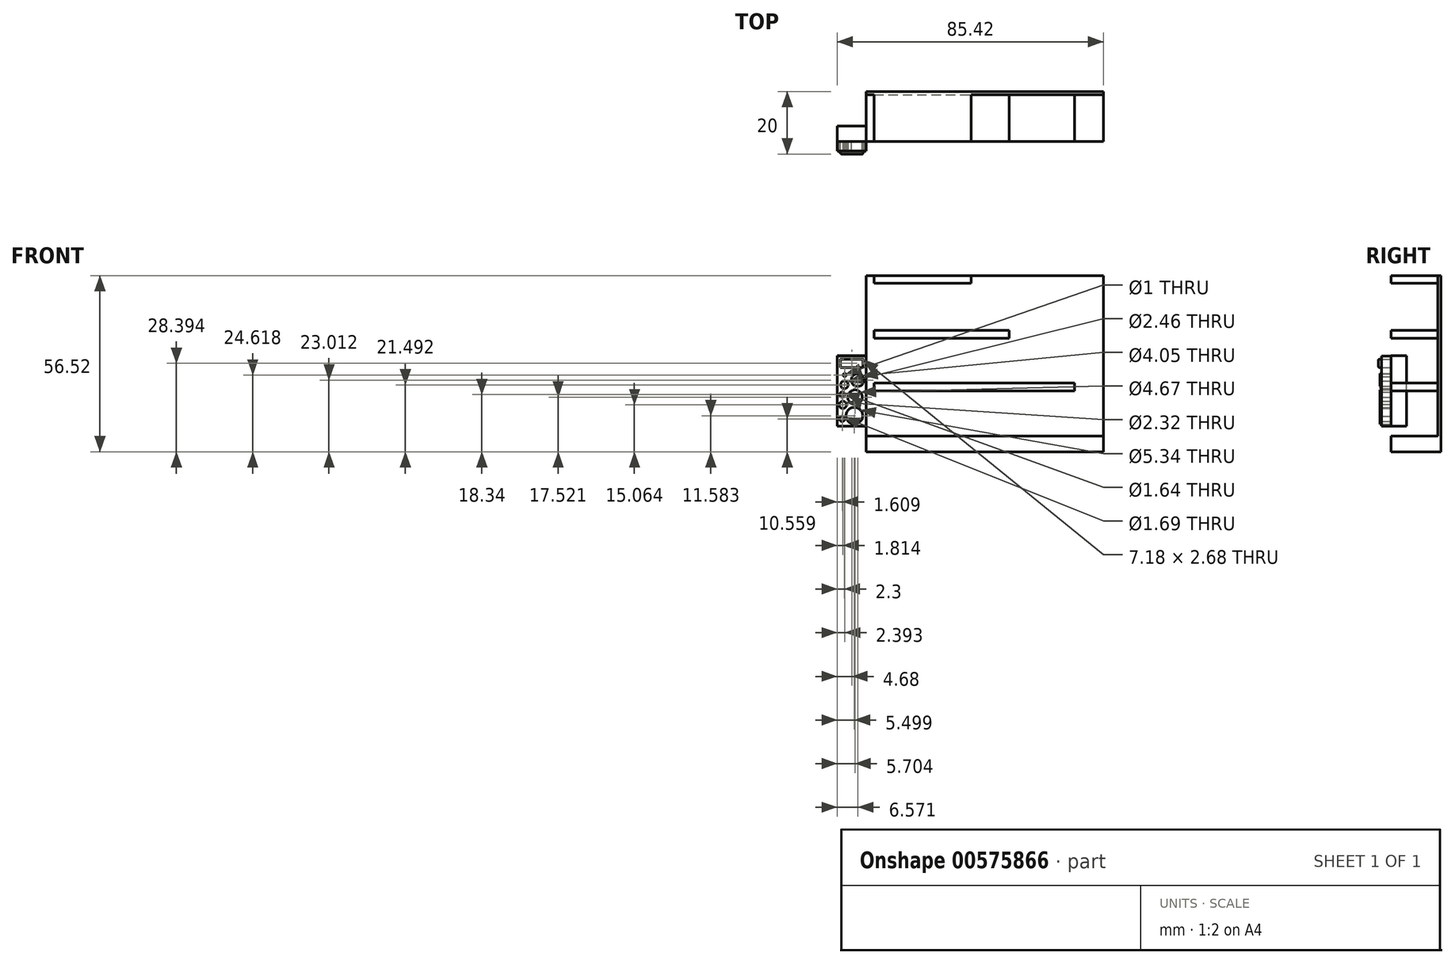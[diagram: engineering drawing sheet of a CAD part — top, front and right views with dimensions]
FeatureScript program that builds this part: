
annotation { "Feature Type Name" : "Feature", "Feature Type Description" : "" }
export const myFeature = defineFeature(function(context is Context, id is Id, definition is map)
    precondition{}
    {
        {
            var Q0;
            Q0=qCreatedBy(makeId("Front.planeOp"),FACE);
            var sketch = newSketch(context, id + "F0", { "sketchPlane" : qUnion([Q0])});
            skLineSegment(sketch, "E0.bottom", {"start": v(-35.88, 0.48) * mm, "end": v(40.2, 0.48) * mm});
            skLineSegment(sketch, "E0.top", {"start": v(-35.88, -4.52) * mm, "end": v(40.2, -4.52) * mm});
            skLineSegment(sketch, "E0.left", {"start": v(-35.88, 0.48) * mm, "end": v(-35.88, -4.52) * mm});
            skLineSegment(sketch, "E0.right", {"start": v(40.2, 0.48) * mm, "end": v(40.2, -4.52) * mm});
            skLineSegment(sketch, "E1.bottom", {"start": v(-35.88, 0.48) * mm, "end": v(-33.38, 0.48) * mm});
            skLineSegment(sketch, "E1.top", {"start": v(-35.88, 52) * mm, "end": v(-33.38, 52) * mm});
            skLineSegment(sketch, "E1.left", {"start": v(-35.88, 0.48) * mm, "end": v(-35.88, 52) * mm});
            skLineSegment(sketch, "E1.right", {"start": v(-33.38, 0.48) * mm, "end": v(-33.38, 52) * mm});
            skLineSegment(sketch, "E2.bottom", {"start": v(-33.38, 52) * mm, "end": v(-2.33, 52) * mm});
            skLineSegment(sketch, "E2.top", {"start": v(-33.38, 49.5) * mm, "end": v(-2.33, 49.5) * mm});
            skLineSegment(sketch, "E2.left", {"start": v(-33.38, 52) * mm, "end": v(-33.38, 49.5) * mm});
            skLineSegment(sketch, "E2.right", {"start": v(-2.33, 52) * mm, "end": v(-2.33, 49.5) * mm});
            skLineSegment(sketch, "E3.bottom", {"start": v(-33.38, 34.4) * mm, "end": v(9.95, 34.4) * mm});
            skLineSegment(sketch, "E3.top", {"start": v(-33.38, 31.9) * mm, "end": v(9.95, 31.9) * mm});
            skLineSegment(sketch, "E3.left", {"start": v(-33.38, 34.4) * mm, "end": v(-33.38, 31.9) * mm});
            skLineSegment(sketch, "E3.right", {"start": v(9.95, 34.4) * mm, "end": v(9.95, 31.9) * mm});
            skLineSegment(sketch, "E4.bottom", {"start": v(-33.38, 17.54) * mm, "end": v(30.82, 17.54) * mm});
            skLineSegment(sketch, "E4.top", {"start": v(-33.38, 15.04) * mm, "end": v(30.82, 15.04) * mm});
            skLineSegment(sketch, "E4.left", {"start": v(-33.38, 17.54) * mm, "end": v(-33.38, 15.04) * mm});
            skLineSegment(sketch, "E4.right", {"start": v(30.82, 17.54) * mm, "end": v(30.82, 15.04) * mm});
            skLineSegment(sketch, "E5.bottom", {"start": v(-35.88, 26.24) * mm, "end": v(-45.17, 26.24) * mm});
            skLineSegment(sketch, "E5.top", {"start": v(-35.88, 3.75) * mm, "end": v(-45.17, 3.75) * mm});
            skLineSegment(sketch, "E5.left", {"start": v(-35.88, 26.24) * mm, "end": v(-35.88, 3.75) * mm});
            skLineSegment(sketch, "E5.right", {"start": v(-45.17, 26.24) * mm, "end": v(-45.17, 3.75) * mm});
            skLineSegment(sketch, "E6.bottom", {"start": v(-44.12, 25.21) * mm, "end": v(-36.94, 25.21) * mm});
            skLineSegment(sketch, "E6.top", {"start": v(-44.12, 22.53) * mm, "end": v(-36.94, 22.53) * mm});
            skLineSegment(sketch, "E6.left", {"start": v(-44.12, 25.21) * mm, "end": v(-44.12, 22.53) * mm});
            skLineSegment(sketch, "E6.right", {"start": v(-36.94, 25.21) * mm, "end": v(-36.94, 22.53) * mm});
            skCircle(sketch, "E7", {"center": v(-42.82, 20.1) * mm, "radius": 0.5 * mm});
            skCircle(sketch, "E8", {"center": v(-42.9, 16.97) * mm, "radius": 1.23 * mm});
            skCircle(sketch, "E9", {"center": v(-38.64, 18.5) * mm, "radius": 2.03 * mm});
            skCircle(sketch, "E10", {"center": v(-39.5, 13) * mm, "radius": 2.33 * mm});
            skCircle(sketch, "E11", {"center": v(-43.4, 10.54) * mm, "radius": 1.16 * mm});
            skCircle(sketch, "E12", {"center": v(-39.71, 7.06) * mm, "radius": 2.67 * mm});
            skCircle(sketch, "E13", {"center": v(-43.6, 13.82) * mm, "radius": 0.82 * mm});
            skCircle(sketch, "E14", {"center": v(-43.6, 6.04) * mm, "radius": 0.84 * mm});
            skSolve(sketch);
        }
        {
            var Q0;
            Q0=makeQuery(id+"F0.imprint","IMPRINT",FACE,{"disambiguationData":[TD([[makeQuery(id+"F0.imprint","IMPRINT",EDGE,{"derivedFrom":sQuery(id+"F0.wireOp",EDGE,"E9")}),1.0]])]});
            var Q1;
            Q1=makeQuery(id+"F0.imprint","IMPRINT",FACE,{"disambiguationData":[TD([[makeQuery(id+"F0.imprint","IMPRINT",EDGE,{"derivedFrom":sQuery(id+"F0.wireOp",EDGE,"E7")}),1.0]])]});
            var Q2;
            Q2=makeQuery(id+"F0.imprint","IMPRINT",FACE,{"disambiguationData":[TD([[makeQuery(id+"F0.imprint","IMPRINT",EDGE,{"derivedFrom":sQuery(id+"F0.wireOp",EDGE,"E8")}),1.0]])]});
            var Q3;
            Q3=makeQuery(id+"F0.imprint","IMPRINT",FACE,{"disambiguationData":[TD([[makeQuery(id+"F0.imprint","IMPRINT",EDGE,{"derivedFrom":sQuery(id+"F0.wireOp",EDGE,"E10")}),1.0]])]});
            var Q4;
            Q4=makeQuery(id+"F0.imprint","IMPRINT",FACE,{"disambiguationData":[TD([[makeQuery(id+"F0.imprint","IMPRINT",EDGE,{"derivedFrom":sQuery(id+"F0.wireOp",EDGE,"E13")}),1.0]])]});
            var Q5;
            Q5=makeQuery(id+"F0.imprint","IMPRINT",FACE,{"disambiguationData":[TD([[makeQuery(id+"F0.imprint","IMPRINT",EDGE,{"derivedFrom":sQuery(id+"F0.wireOp",EDGE,"E11")}),1.0]])]});
            var Q6;
            Q6=makeQuery(id+"F0.imprint","IMPRINT",FACE,{"disambiguationData":[TD([[makeQuery(id+"F0.imprint","IMPRINT",EDGE,{"derivedFrom":sQuery(id+"F0.wireOp",EDGE,"E12")}),1.0]])]});
            var Q7;
            Q7=makeQuery(id+"F0.imprint","IMPRINT",FACE,{"disambiguationData":[TD([[makeQuery(id+"F0.imprint","IMPRINT",EDGE,{"derivedFrom":sQuery(id+"F0.wireOp",EDGE,"E14")}),1.0]])]});
            extrude(context, id + "F1", {"entities" : qUnion([Q0, Q1, Q2, Q3, Q4, Q5, Q6, Q7]), "depth" : 3.5 * mm, "offsetDistance" : 25.4 * mm});
        }
        {
            var Q0;
            Q0=makeQuery(id+"F0.imprint","IMPRINT",FACE,{"disambiguationData":[TD([[makeQuery(id+"F0.imprint","IMPRINT",EDGE,{"derivedFrom":sQuery(id+"F0.wireOp",EDGE,"E6.bottom")}),-1.0]])]});
            extrude(context, id + "F2", {"entities" : qUnion([Q0]), "depth" : 4 * mm, "offsetDistance" : 25.4 * mm});
        }
        {
            var Q0;
            Q0=makeQuery(id+"F0.imprint","IMPRINT",FACE,{"disambiguationData":[TD([[makeQuery(id+"F0.imprint","IMPRINT",EDGE,{"derivedFrom":sQuery(id+"F0.wireOp",EDGE,"E5.bottom")}),1.0]])]});
            extrude(context, id + "F3", {"entities" : qUnion([Q0]), "depth" : 3 * mm, "offsetDistance" : 25.4 * mm});
        }
        {
            var Q0;
            Q0=makeQuery(id+"F0.imprint","IMPRINT",FACE,{"disambiguationData":[TD([[makeQuery(id+"F0.imprint","IMPRINT",EDGE,{"derivedFrom":sQuery(id+"F0.wireOp",EDGE,"E3.bottom")}),-1.0]])]});
            var Q1;
            Q1=makeQuery(id+"F0.imprint","IMPRINT",FACE,{"disambiguationData":[TD([[makeQuery(id+"F0.imprint","IMPRINT",EDGE,{"derivedFrom":sQuery(id+"F0.wireOp",EDGE,"E2.bottom")}),-1.0]])]});
            var Q2;
            {var subQ4=sQuery(id+"F0.wireOp",EDGE,"E1.bottom");Q2=makeQuery(id+"F0.imprint","IMPRINT",FACE,{"disambiguationData":[TD([[makeQuery(id+"F0.imprint","IMPRINT",EDGE,{"derivedFrom":subQ4}),1.0]])]});}
            var Q3;
            Q3=makeQuery(id+"F0.imprint","IMPRINT",FACE,{"disambiguationData":[TD([[makeQuery(id+"F0.imprint","IMPRINT",EDGE,{"derivedFrom":sQuery(id+"F0.wireOp",EDGE,"E4.bottom")}),-1.0]])]});
            var Q4;
            Q4=makeQuery(id+"F0.imprint","IMPRINT",FACE,{"disambiguationData":[TD([[makeQuery(id+"F0.imprint","IMPRINT",EDGE,{"derivedFrom":sQuery(id+"F0.wireOp",EDGE,"E0.bottom")}),-1.0]])]});
            extrude(context, id + "F4", {"entities" : qUnion([Q0, Q1, Q2, Q3, Q4]), "oppositeDirection" : true, "depth" : 15 * mm, "offsetDistance" : 25.4 * mm});
        }
        {
            var Q0;
            Q0=makeQuery(id+"F4.opExtrude","CAP_FACE",FACE,{"disambiguationData":[OSD([sQuery(id+"F0.wireOp",EDGE,"E0.bottom"),sQuery(id+"F0.wireOp",EDGE,"E0.top"),sQuery(id+"F0.wireOp",EDGE,"E0.left"),sQuery(id+"F0.wireOp",EDGE,"E0.right"),sQuery(id+"F0.wireOp",EDGE,"E1.top"),sQuery(id+"F0.wireOp",EDGE,"E1.left"),sQuery(id+"F0.wireOp",EDGE,"E1.right"),sQuery(id+"F0.wireOp",EDGE,"E2.bottom"),sQuery(id+"F0.wireOp",EDGE,"E2.top"),sQuery(id+"F0.wireOp",EDGE,"E2.right"),sQuery(id+"F0.wireOp",EDGE,"E3.bottom"),sQuery(id+"F0.wireOp",EDGE,"E3.top"),sQuery(id+"F0.wireOp",EDGE,"E3.right"),sQuery(id+"F0.wireOp",EDGE,"E4.bottom"),sQuery(id+"F0.wireOp",EDGE,"E4.top"),sQuery(id+"F0.wireOp",EDGE,"E4.right"),sQuery(id+"F0.wireOp",EDGE,"E5.left")])],"isStart":false});
            var sketch = newSketch(context, id + "F5", { "sketchPlane" : qUnion([Q0])});
            skLineSegment(sketch, "E15.bottom", {"start": v(35.88, 52) * mm, "end": v(-40.2, 52) * mm});
            skLineSegment(sketch, "E15.top", {"start": v(35.88, -4.52) * mm, "end": v(-40.2, -4.52) * mm});
            skLineSegment(sketch, "E15.left", {"start": v(35.88, 52) * mm, "end": v(35.88, -4.52) * mm});
            skLineSegment(sketch, "E15.right", {"start": v(-40.2, 52) * mm, "end": v(-40.2, -4.52) * mm});
            skSolve(sketch);
        }
        {
            var Q0;
            Q0 = qSketchRegion(id + "F5", true);
            extrude(context, id + "F6", {"entities" : qUnion([Q0]), "operationType" : NewBodyOperationType.ADD, "depth" : 1 * mm, "offsetDistance" : 25.4 * mm});
        }
        {
            var Q0;
            Q0=makeQuery(id+"F2.opExtrude","CAP_EDGE",EDGE,{"disambiguationData":[OSD([sQuery(id+"F0.wireOp",EDGE,"E6.top")])],"isStart":false});
            var Q1;
            Q1=makeQuery(id+"F2.opExtrude","CAP_EDGE",EDGE,{"disambiguationData":[OSD([sQuery(id+"F0.wireOp",EDGE,"E6.bottom")])],"isStart":false});
            var Q2;
            Q2=makeQuery(id+"F2.opExtrude","CAP_EDGE",EDGE,{"disambiguationData":[OSD([sQuery(id+"F0.wireOp",EDGE,"E6.right")])],"isStart":false});
            var Q3;
            Q3=makeQuery(id+"F2.opExtrude","CAP_EDGE",EDGE,{"disambiguationData":[OSD([sQuery(id+"F0.wireOp",EDGE,"E6.left")])],"isStart":false});
            fillet(context, id + "F7", {"entities" : qUnion([Q0, Q1, Q2, Q3]), "radius" : 0.25 * mm, "tangentPropagation" : true, "allowEdgeOverflow" : false});
        }
        {
            var Q0;
            Q0=makeQuery(id+"F0.imprint","IMPRINT",FACE,{"disambiguationData":[TD([[makeQuery(id+"F0.imprint","IMPRINT",EDGE,{"derivedFrom":sQuery(id+"F0.wireOp",EDGE,"E5.bottom")}),1.0]])]});
            var sketch = newSketch(context, id + "F8", { "sketchPlane" : qUnion([Q0])});
            skLineSegment(sketch, "E16.bottom", {"start": v(-45.2, 3.72) * mm, "end": v(-35.92, 3.72) * mm});
            skLineSegment(sketch, "E16.top", {"start": v(-45.2, 26.28) * mm, "end": v(-35.92, 26.28) * mm});
            skLineSegment(sketch, "E16.left", {"start": v(-45.2, 3.72) * mm, "end": v(-45.2, 26.28) * mm});
            skLineSegment(sketch, "E16.right", {"start": v(-35.92, 3.72) * mm, "end": v(-35.92, 26.28) * mm});
            skSolve(sketch);
        }
        {
            var Q0;
            Q0 = qSketchRegion(id + "F8", true);
            extrude(context, id + "F9", {"entities" : qUnion([Q0]), "oppositeDirection" : true, "depth" : 5 * mm, "offsetDistance" : 25.4 * mm});
        }
    });
